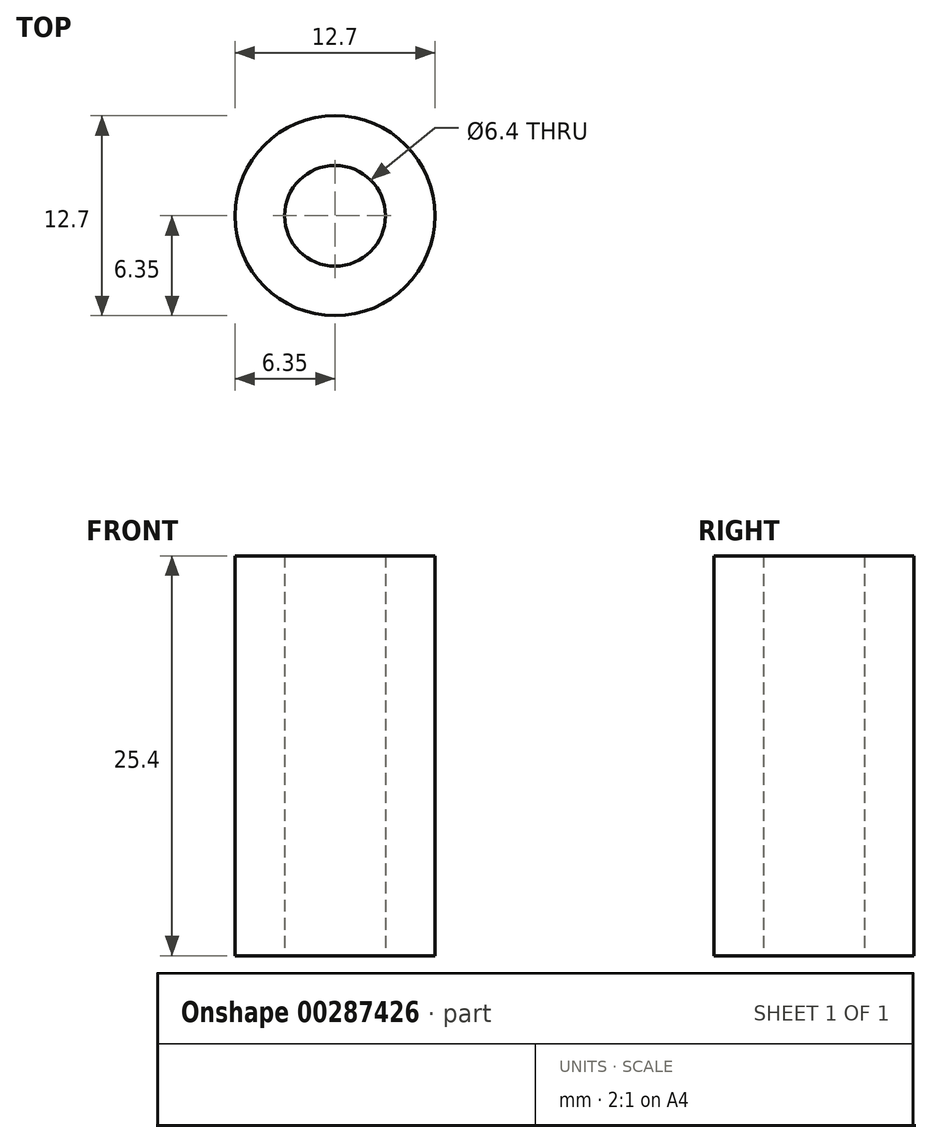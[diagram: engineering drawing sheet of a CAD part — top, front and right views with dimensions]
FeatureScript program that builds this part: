
annotation { "Feature Type Name" : "Feature", "Feature Type Description" : "" }
export const myFeature = defineFeature(function(context is Context, id is Id, definition is map)
    precondition{}
    {
        {
            var Q0;
            Q0=qCreatedBy(makeId("Top.planeOp"),FACE);
            var sketch = newSketch(context, id + "F0", { "sketchPlane" : qUnion([Q0])});
            skCircle(sketch, "E0", {"center": v(0, 0) * mm, "radius": 6.35 * mm});
            skCircle(sketch, "E1", {"center": v(0, 0) * mm, "radius": 3.2 * mm});
            skSolve(sketch);
        }
        {
            var Q0;
            Q0=makeQuery(id+"F0.imprint","IMPRINT",FACE,{"disambiguationData":[TD([[makeQuery(id+"F0.imprint","IMPRINT",EDGE,{"derivedFrom":sQuery(id+"F0.wireOp",EDGE,"E0")}),1.0]])]});
            extrude(context, id + "F1", {"entities" : qUnion([Q0]), "depth" : 25.4 * mm, "offsetDistance" : 25.4 * mm});
        }
    });
